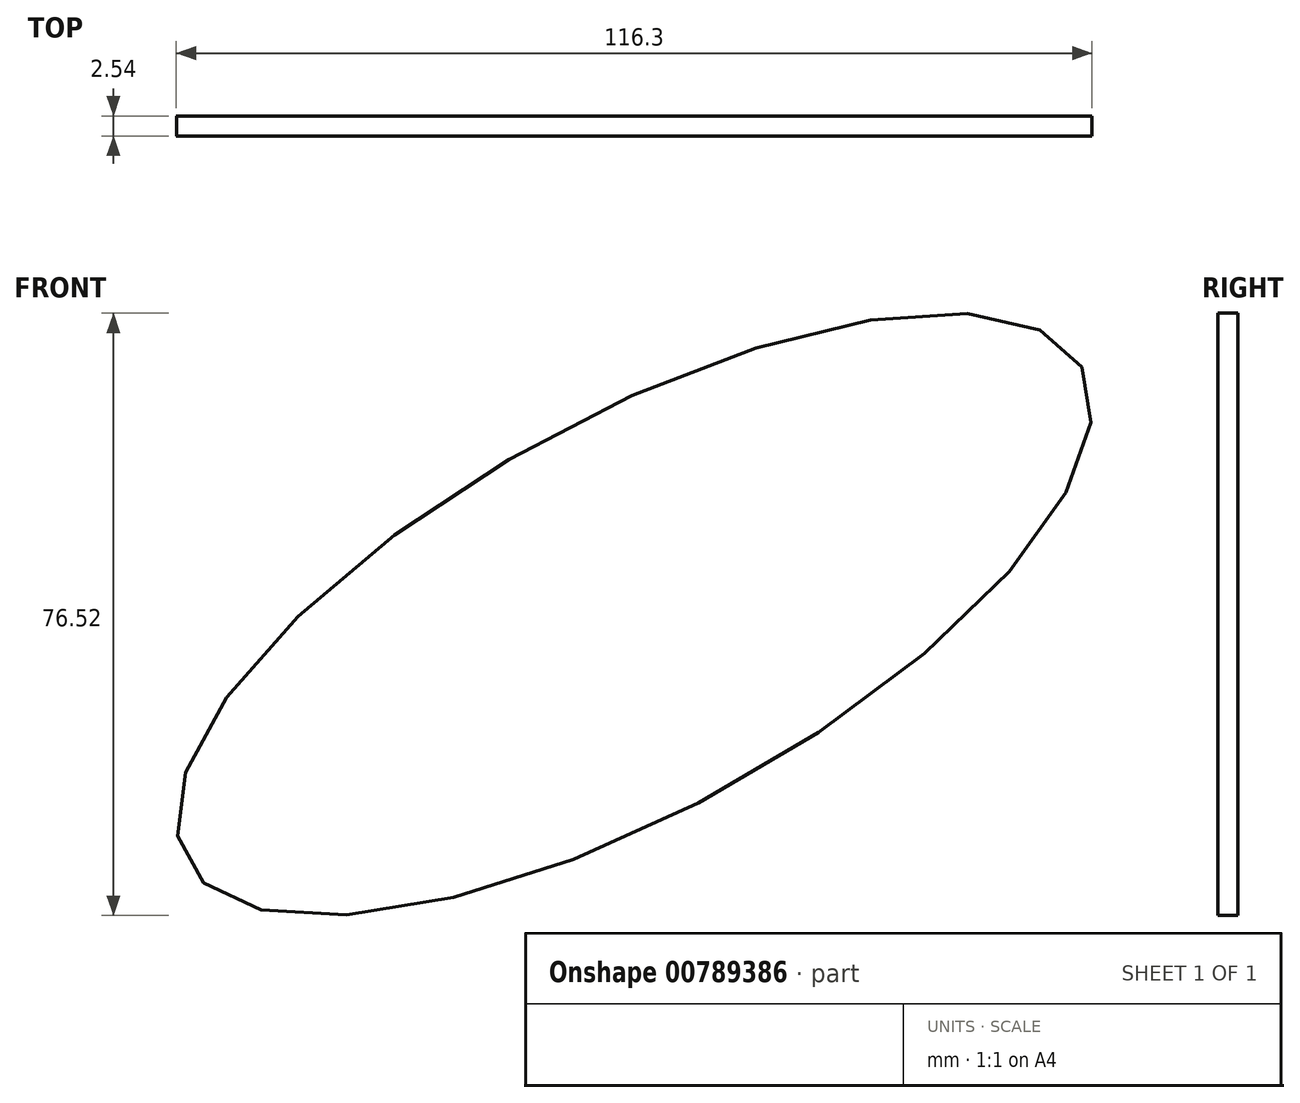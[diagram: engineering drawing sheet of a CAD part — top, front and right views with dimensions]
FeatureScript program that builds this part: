
annotation { "Feature Type Name" : "Feature", "Feature Type Description" : "" }
export const myFeature = defineFeature(function(context is Context, id is Id, definition is map)
    precondition{}
    {
        {
            var Q0;
            Q0=qCreatedBy(makeId("Front.planeOp"),FACE);
            var sketch = newSketch(context, id + "F0", { "sketchPlane" : qUnion([Q0])});
            skEllipse(sketch, "E0", {"center": v(0, 0) * mm, "majorRadius": 64.98 * mm, "minorRadius": 24.96 * mm, "majorAxis": v(0.88, 0.48)});
            skSolve(sketch);
        }
        {
            var Q0;
            Q0=makeQuery(id+"F0.imprint","IMPRINT",FACE,{"disambiguationData":[TD([[makeQuery(id+"F0.imprint","IMPRINT",EDGE,{"derivedFrom":sQuery(id+"F0.wireOp",EDGE,"E0")}),1.0]])]});
            var Q1;
            Q1=sQuery(id+"F0.wireOp",EDGE,"E0");
            extrude(context, id + "F1", {"entities" : qUnion([Q0]), "bodyType" : ToolBodyType.SURFACE, "surfaceEntities" : qUnion([Q1]), "depth" : 2.54 * mm, "offsetDistance" : 25.4 * mm});
        }
    });
